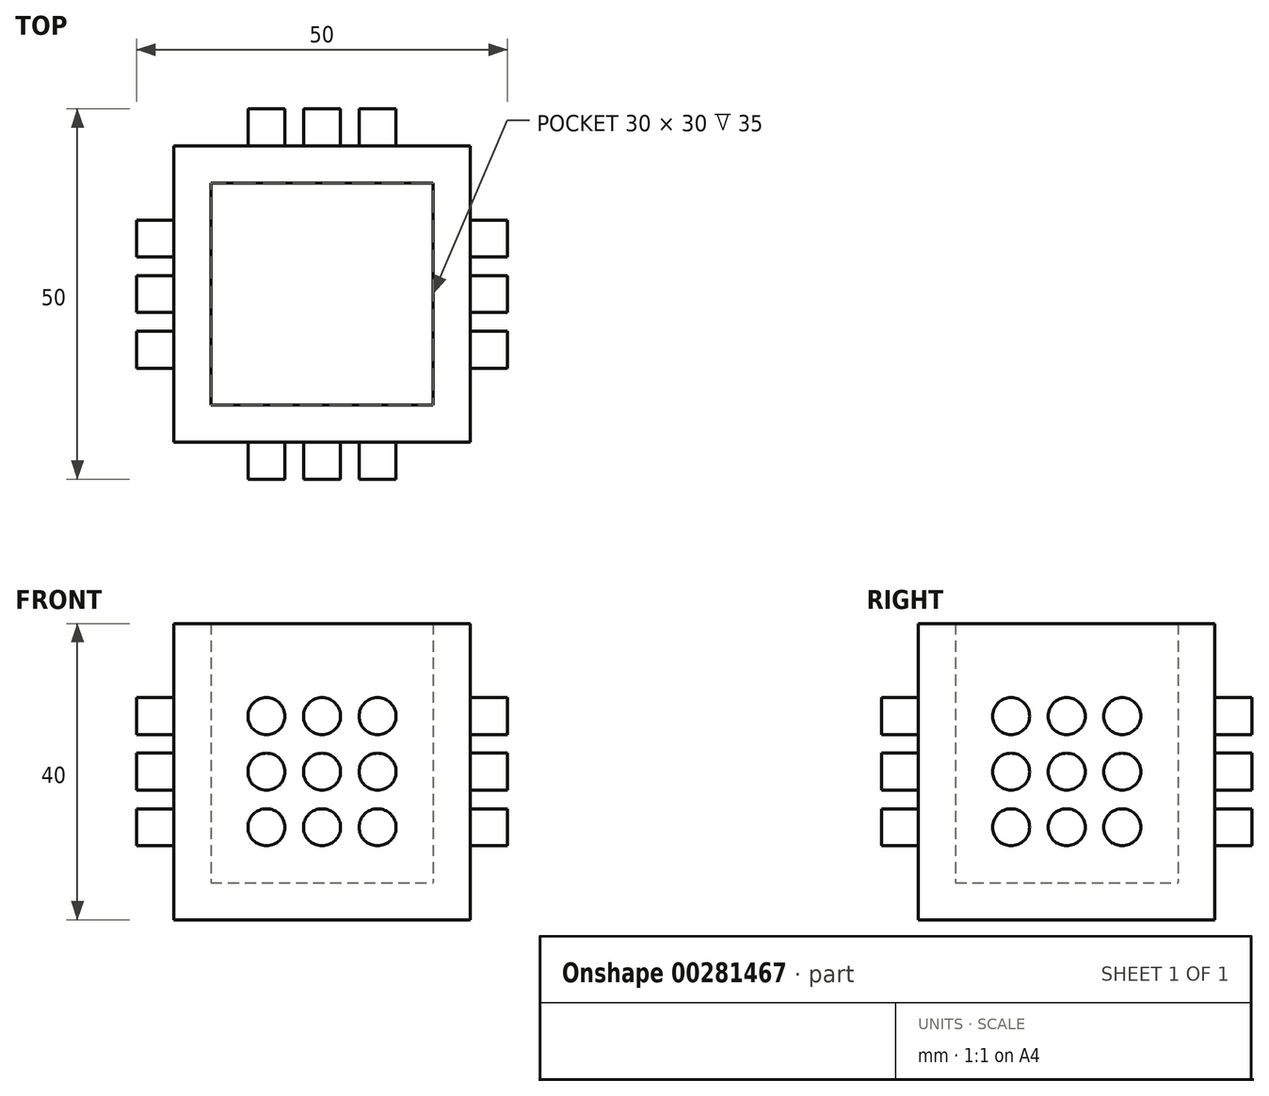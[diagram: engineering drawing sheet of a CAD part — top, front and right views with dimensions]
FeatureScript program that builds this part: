
annotation { "Feature Type Name" : "Feature", "Feature Type Description" : "" }
export const myFeature = defineFeature(function(context is Context, id is Id, definition is map)
    precondition{}
    {
        {
            var Q0;
            Q0=qCreatedBy(makeId("Top.planeOp"),FACE);
            var sketch = newSketch(context, id + "F0", { "sketchPlane" : qUnion([Q0])});
            skLineSegment(sketch, "E0.bottom", {"start": v(0, 0) * mm, "end": v(40, 0) * mm});
            skLineSegment(sketch, "E0.top", {"start": v(0, 40) * mm, "end": v(40, 40) * mm});
            skLineSegment(sketch, "E0.left", {"start": v(0, 0) * mm, "end": v(0, 40) * mm});
            skLineSegment(sketch, "E0.right", {"start": v(40, 0) * mm, "end": v(40, 40) * mm});
            skLineSegment(sketch, "E1.bottom", {"start": v(5, 5) * mm, "end": v(35, 5) * mm});
            skLineSegment(sketch, "E1.top", {"start": v(5, 35) * mm, "end": v(35, 35) * mm});
            skLineSegment(sketch, "E1.left", {"start": v(5, 5) * mm, "end": v(5, 35) * mm});
            skLineSegment(sketch, "E1.right", {"start": v(35, 5) * mm, "end": v(35, 35) * mm});
            skSolve(sketch);
        }
        {
            var Q0;
            Q0=makeQuery(id+"F0.imprint","IMPRINT",FACE,{"disambiguationData":[TD([[makeQuery(id+"F0.imprint","IMPRINT",EDGE,{"derivedFrom":sQuery(id+"F0.wireOp",EDGE,"E0.bottom")}),1.0]])]});
            var Q1;
            Q1=makeQuery(id+"F0.imprint","IMPRINT",FACE,{"disambiguationData":[TD([[makeQuery(id+"F0.imprint","IMPRINT",EDGE,{"derivedFrom":sQuery(id+"F0.wireOp",EDGE,"E1.bottom")}),1.0]])]});
            extrude(context, id + "F1", {"entities" : qUnion([Q0, Q1]), "depth" : 5 * mm});
        }
        {
            var Q0;
            Q0=makeQuery(id+"F1.opExtrude","CAP_FACE",FACE,{"disambiguationData":[OSD([sQuery(id+"F0.wireOp",EDGE,"E0.bottom"),sQuery(id+"F0.wireOp",EDGE,"E0.top"),sQuery(id+"F0.wireOp",EDGE,"E0.left"),sQuery(id+"F0.wireOp",EDGE,"E0.right")])],"isStart":false});
            var sketch = newSketch(context, id + "F2", { "sketchPlane" : qUnion([Q0])});
            skLineSegment(sketch, "E2.bottom", {"start": v(5, 5) * mm, "end": v(35, 5) * mm});
            skLineSegment(sketch, "E2.top", {"start": v(5, 35) * mm, "end": v(35, 35) * mm});
            skLineSegment(sketch, "E2.left", {"start": v(5, 5) * mm, "end": v(5, 35) * mm});
            skLineSegment(sketch, "E2.right", {"start": v(35, 5) * mm, "end": v(35, 35) * mm});
            skSolve(sketch);
        }
        {
            var Q0;
            Q0=makeQuery(id+"F2.imprint","IMPRINT",FACE,{"disambiguationData":[TD([[makeQuery(id+"F2.imprint","IMPRINT",EDGE,{"derivedFrom":sQuery(id+"F2.wireOp",EDGE,"E2.bottom")}),-1.0]])]});
            extrude(context, id + "F3", {"entities" : qUnion([Q0]), "operationType" : NewBodyOperationType.ADD, "depth" : 35 * mm});
        }
        {
            var Q0;
            Q0=qCreatedBy(makeId("Front.planeOp"),FACE);
            var sketch = newSketch(context, id + "F4", { "sketchPlane" : qUnion([Q0])});
            skLineSegment(sketch, "E3.bottom", {"start": v(5, 5) * mm, "end": v(35, 5) * mm});
            skLineSegment(sketch, "E3.top", {"start": v(5, 35) * mm, "end": v(35, 35) * mm});
            skLineSegment(sketch, "E3.left", {"start": v(5, 5) * mm, "end": v(5, 35) * mm});
            skLineSegment(sketch, "E3.right", {"start": v(35, 5) * mm, "end": v(35, 35) * mm});
            skLineSegment(sketch, "E4", {"start": v(12.5, 5) * mm, "end": v(12.5, 10) * mm});
            skLineSegment(sketch, "E5", {"start": v(20, 5) * mm, "end": v(20, 10) * mm});
            skLineSegment(sketch, "E6", {"start": v(27.5, 5) * mm, "end": v(27.5, 10) * mm});
            skLineSegment(sketch, "E7", {"start": v(5, 27.5) * mm, "end": v(10, 27.5) * mm});
            skLineSegment(sketch, "E8", {"start": v(5, 20) * mm, "end": v(10, 20) * mm});
            skLineSegment(sketch, "E9", {"start": v(5, 12.5) * mm, "end": v(10, 12.5) * mm});
            skCircle(sketch, "E10", {"center": v(12.5, 27.5) * mm, "radius": 2.5 * mm});
            skCircle(sketch, "E11", {"center": v(20, 27.5) * mm, "radius": 2.5 * mm});
            skCircle(sketch, "E12", {"center": v(27.5, 27.5) * mm, "radius": 2.5 * mm});
            skCircle(sketch, "E13", {"center": v(27.5, 20) * mm, "radius": 2.5 * mm});
            skCircle(sketch, "E14", {"center": v(20, 20) * mm, "radius": 2.5 * mm});
            skCircle(sketch, "E15", {"center": v(12.5, 20) * mm, "radius": 2.5 * mm});
            skCircle(sketch, "E16", {"center": v(12.5, 12.5) * mm, "radius": 2.5 * mm});
            skCircle(sketch, "E17", {"center": v(20, 12.5) * mm, "radius": 2.5 * mm});
            skCircle(sketch, "E18", {"center": v(27.5, 12.5) * mm, "radius": 2.5 * mm});
            skLineSegment(sketch, "E19.trimOffspring", {"start": v(12.5, 30) * mm, "end": v(12.5, 35) * mm});
            skLineSegment(sketch, "E20.trimOffspring", {"start": v(15, 27.5) * mm, "end": v(17.5, 27.5) * mm});
            skLineSegment(sketch, "E21.trimOffspring", {"start": v(22.5, 27.5) * mm, "end": v(25, 27.5) * mm});
            skLineSegment(sketch, "E22.trimOffspring", {"start": v(20, 30) * mm, "end": v(20, 35) * mm});
            skLineSegment(sketch, "E23.trimOffspring", {"start": v(30, 27.5) * mm, "end": v(35, 27.5) * mm});
            skLineSegment(sketch, "E24.trimOffspring", {"start": v(27.5, 30) * mm, "end": v(27.5, 35) * mm});
            skLineSegment(sketch, "E25.trimOffspring", {"start": v(12.5, 22.5) * mm, "end": v(12.5, 25) * mm});
            skLineSegment(sketch, "E26.trimOffspring", {"start": v(15, 20) * mm, "end": v(17.5, 20) * mm});
            skLineSegment(sketch, "E27.trimOffspring", {"start": v(22.5, 20) * mm, "end": v(25, 20) * mm});
            skLineSegment(sketch, "E28.trimOffspring", {"start": v(20, 22.5) * mm, "end": v(20, 25) * mm});
            skLineSegment(sketch, "E29.trimOffspring", {"start": v(30, 20) * mm, "end": v(35, 20) * mm});
            skLineSegment(sketch, "E30.trimOffspring", {"start": v(27.5, 22.5) * mm, "end": v(27.5, 25) * mm});
            skLineSegment(sketch, "E31.trimOffspring", {"start": v(12.5, 15) * mm, "end": v(12.5, 17.5) * mm});
            skLineSegment(sketch, "E32.trimOffspring", {"start": v(15, 12.5) * mm, "end": v(17.5, 12.5) * mm});
            skLineSegment(sketch, "E33.trimOffspring", {"start": v(22.5, 12.5) * mm, "end": v(25, 12.5) * mm});
            skLineSegment(sketch, "E34.trimOffspring", {"start": v(20, 15) * mm, "end": v(20, 17.5) * mm});
            skLineSegment(sketch, "E35.trimOffspring", {"start": v(30, 12.5) * mm, "end": v(35, 12.5) * mm});
            skLineSegment(sketch, "E36.trimOffspring", {"start": v(27.5, 15) * mm, "end": v(27.5, 17.5) * mm});
            skSolve(sketch);
        }
        {
            var Q0;
            {var subQ0=sQuery(id+"F0.wireOp",EDGE,"E0.right");Q0=makeQuery(id+"F3.boolean.opBoolean","MERGE",FACE,{"derivedFrom":[makeQuery(id+"F1.opExtrude","SWEPT_FACE",FACE,{"disambiguationData":[OSD([subQ0])]}),makeQuery(id+"F3.opExtrude","SWEPT_FACE",FACE,{"disambiguationData":[OSD([subQ0])]})]});}
            var sketch = newSketch(context, id + "F5", { "sketchPlane" : qUnion([Q0])});
            skLineSegment(sketch, "E37.bottom", {"start": v(5, 5) * mm, "end": v(35, 5) * mm});
            skLineSegment(sketch, "E37.top", {"start": v(5, 35) * mm, "end": v(35, 35) * mm});
            skLineSegment(sketch, "E37.left", {"start": v(5, 5) * mm, "end": v(5, 35) * mm});
            skLineSegment(sketch, "E37.right", {"start": v(35, 5) * mm, "end": v(35, 35) * mm});
            skLineSegment(sketch, "E38", {"start": v(12.5, 5) * mm, "end": v(12.5, 10) * mm});
            skLineSegment(sketch, "E39", {"start": v(20, 5) * mm, "end": v(20, 10) * mm});
            skLineSegment(sketch, "E40", {"start": v(27.5, 5) * mm, "end": v(27.5, 10) * mm});
            skLineSegment(sketch, "E41", {"start": v(5, 27.5) * mm, "end": v(10, 27.5) * mm});
            skLineSegment(sketch, "E42", {"start": v(5, 20) * mm, "end": v(10, 20) * mm});
            skLineSegment(sketch, "E43", {"start": v(5, 12.5) * mm, "end": v(10, 12.5) * mm});
            skCircle(sketch, "E44", {"center": v(12.5, 27.5) * mm, "radius": 2.5 * mm});
            skCircle(sketch, "E45", {"center": v(20, 27.5) * mm, "radius": 2.5 * mm});
            skCircle(sketch, "E46", {"center": v(27.5, 27.5) * mm, "radius": 2.5 * mm});
            skCircle(sketch, "E47", {"center": v(27.5, 20) * mm, "radius": 2.5 * mm});
            skCircle(sketch, "E48", {"center": v(20, 20) * mm, "radius": 2.5 * mm});
            skCircle(sketch, "E49", {"center": v(12.5, 20) * mm, "radius": 2.5 * mm});
            skCircle(sketch, "E50", {"center": v(12.5, 12.5) * mm, "radius": 2.5 * mm});
            skCircle(sketch, "E51", {"center": v(20, 12.5) * mm, "radius": 2.5 * mm});
            skCircle(sketch, "E52", {"center": v(27.5, 12.5) * mm, "radius": 2.5 * mm});
            skLineSegment(sketch, "E53.trimOffspring", {"start": v(12.5, 30) * mm, "end": v(12.5, 35) * mm});
            skLineSegment(sketch, "E54.trimOffspring", {"start": v(15, 27.5) * mm, "end": v(17.5, 27.5) * mm});
            skLineSegment(sketch, "E55.trimOffspring", {"start": v(22.5, 27.5) * mm, "end": v(25, 27.5) * mm});
            skLineSegment(sketch, "E56.trimOffspring", {"start": v(20, 30) * mm, "end": v(20, 35) * mm});
            skLineSegment(sketch, "E57.trimOffspring", {"start": v(30, 27.5) * mm, "end": v(35, 27.5) * mm});
            skLineSegment(sketch, "E58.trimOffspring", {"start": v(27.5, 30) * mm, "end": v(27.5, 35) * mm});
            skLineSegment(sketch, "E59.trimOffspring", {"start": v(12.5, 22.5) * mm, "end": v(12.5, 25) * mm});
            skLineSegment(sketch, "E60.trimOffspring", {"start": v(15, 20) * mm, "end": v(17.5, 20) * mm});
            skLineSegment(sketch, "E61.trimOffspring", {"start": v(22.5, 20) * mm, "end": v(25, 20) * mm});
            skLineSegment(sketch, "E62.trimOffspring", {"start": v(20, 22.5) * mm, "end": v(20, 25) * mm});
            skLineSegment(sketch, "E63.trimOffspring", {"start": v(30, 20) * mm, "end": v(35, 20) * mm});
            skLineSegment(sketch, "E64.trimOffspring", {"start": v(27.5, 22.5) * mm, "end": v(27.5, 25) * mm});
            skLineSegment(sketch, "E65.trimOffspring", {"start": v(12.5, 15) * mm, "end": v(12.5, 17.5) * mm});
            skLineSegment(sketch, "E66.trimOffspring", {"start": v(15, 12.5) * mm, "end": v(17.5, 12.5) * mm});
            skLineSegment(sketch, "E67.trimOffspring", {"start": v(22.5, 12.5) * mm, "end": v(25, 12.5) * mm});
            skLineSegment(sketch, "E68.trimOffspring", {"start": v(20, 15) * mm, "end": v(20, 17.5) * mm});
            skLineSegment(sketch, "E69.trimOffspring", {"start": v(30, 12.5) * mm, "end": v(35, 12.5) * mm});
            skLineSegment(sketch, "E70.trimOffspring", {"start": v(27.5, 15) * mm, "end": v(27.5, 17.5) * mm});
            skSolve(sketch);
        }
        {
            var Q0;
            {var subQ0=sQuery(id+"F0.wireOp",EDGE,"E0.top");Q0=makeQuery(id+"F3.boolean.opBoolean","MERGE",FACE,{"derivedFrom":[makeQuery(id+"F1.opExtrude","SWEPT_FACE",FACE,{"disambiguationData":[OSD([subQ0])]}),makeQuery(id+"F3.opExtrude","SWEPT_FACE",FACE,{"disambiguationData":[OSD([subQ0])]})]});}
            var sketch = newSketch(context, id + "F6", { "sketchPlane" : qUnion([Q0])});
            skLineSegment(sketch, "E71.bottom", {"start": v(-35, 5) * mm, "end": v(-5, 5) * mm});
            skLineSegment(sketch, "E71.top", {"start": v(-35, 35) * mm, "end": v(-5, 35) * mm});
            skLineSegment(sketch, "E71.left", {"start": v(-35, 5) * mm, "end": v(-35, 35) * mm});
            skLineSegment(sketch, "E71.right", {"start": v(-5, 5) * mm, "end": v(-5, 35) * mm});
            skLineSegment(sketch, "E72", {"start": v(-27.5, 5) * mm, "end": v(-27.5, 10) * mm});
            skLineSegment(sketch, "E73", {"start": v(-20, 5) * mm, "end": v(-20, 10) * mm});
            skLineSegment(sketch, "E74", {"start": v(-12.5, 5) * mm, "end": v(-12.5, 10) * mm});
            skLineSegment(sketch, "E75", {"start": v(-35, 27.5) * mm, "end": v(-30, 27.5) * mm});
            skLineSegment(sketch, "E76", {"start": v(-35, 20) * mm, "end": v(-30, 20) * mm});
            skLineSegment(sketch, "E77", {"start": v(-35, 12.5) * mm, "end": v(-30, 12.5) * mm});
            skCircle(sketch, "E78", {"center": v(-27.5, 27.5) * mm, "radius": 2.5 * mm});
            skCircle(sketch, "E79", {"center": v(-20, 27.5) * mm, "radius": 2.5 * mm});
            skCircle(sketch, "E80", {"center": v(-12.5, 27.5) * mm, "radius": 2.5 * mm});
            skCircle(sketch, "E81", {"center": v(-12.5, 20) * mm, "radius": 2.5 * mm});
            skCircle(sketch, "E82", {"center": v(-20, 20) * mm, "radius": 2.5 * mm});
            skCircle(sketch, "E83", {"center": v(-27.5, 20) * mm, "radius": 2.5 * mm});
            skCircle(sketch, "E84", {"center": v(-27.5, 12.5) * mm, "radius": 2.5 * mm});
            skCircle(sketch, "E85", {"center": v(-20, 12.5) * mm, "radius": 2.5 * mm});
            skCircle(sketch, "E86", {"center": v(-12.5, 12.5) * mm, "radius": 2.5 * mm});
            skLineSegment(sketch, "E87.trimOffspring", {"start": v(-27.5, 30) * mm, "end": v(-27.5, 35) * mm});
            skLineSegment(sketch, "E88.trimOffspring", {"start": v(-25, 27.5) * mm, "end": v(-22.5, 27.5) * mm});
            skLineSegment(sketch, "E89.trimOffspring", {"start": v(-17.5, 27.5) * mm, "end": v(-15, 27.5) * mm});
            skLineSegment(sketch, "E90.trimOffspring", {"start": v(-20, 30) * mm, "end": v(-20, 35) * mm});
            skLineSegment(sketch, "E91.trimOffspring", {"start": v(-10, 27.5) * mm, "end": v(-5, 27.5) * mm});
            skLineSegment(sketch, "E92.trimOffspring", {"start": v(-12.5, 30) * mm, "end": v(-12.5, 35) * mm});
            skLineSegment(sketch, "E93.trimOffspring", {"start": v(-27.5, 22.5) * mm, "end": v(-27.5, 25) * mm});
            skLineSegment(sketch, "E94.trimOffspring", {"start": v(-25, 20) * mm, "end": v(-22.5, 20) * mm});
            skLineSegment(sketch, "E95.trimOffspring", {"start": v(-17.5, 20) * mm, "end": v(-15, 20) * mm});
            skLineSegment(sketch, "E96.trimOffspring", {"start": v(-20, 22.5) * mm, "end": v(-20, 25) * mm});
            skLineSegment(sketch, "E97.trimOffspring", {"start": v(-10, 20) * mm, "end": v(-5, 20) * mm});
            skLineSegment(sketch, "E98.trimOffspring", {"start": v(-12.5, 22.5) * mm, "end": v(-12.5, 25) * mm});
            skLineSegment(sketch, "E99.trimOffspring", {"start": v(-27.5, 15) * mm, "end": v(-27.5, 17.5) * mm});
            skLineSegment(sketch, "E100.trimOffspring", {"start": v(-25, 12.5) * mm, "end": v(-22.5, 12.5) * mm});
            skLineSegment(sketch, "E101.trimOffspring", {"start": v(-17.5, 12.5) * mm, "end": v(-15, 12.5) * mm});
            skLineSegment(sketch, "E102.trimOffspring", {"start": v(-20, 15) * mm, "end": v(-20, 17.5) * mm});
            skLineSegment(sketch, "E103.trimOffspring", {"start": v(-10, 12.5) * mm, "end": v(-5, 12.5) * mm});
            skLineSegment(sketch, "E104.trimOffspring", {"start": v(-12.5, 15) * mm, "end": v(-12.5, 17.5) * mm});
            skSolve(sketch);
        }
        {
            var Q0;
            {var subQ0=sQuery(id+"F0.wireOp",EDGE,"E0.left");Q0=makeQuery(id+"F3.boolean.opBoolean","MERGE",FACE,{"derivedFrom":[makeQuery(id+"F1.opExtrude","SWEPT_FACE",FACE,{"disambiguationData":[OSD([subQ0])]}),makeQuery(id+"F3.opExtrude","SWEPT_FACE",FACE,{"disambiguationData":[OSD([subQ0])]})]});}
            var sketch = newSketch(context, id + "F7", { "sketchPlane" : qUnion([Q0])});
            skLineSegment(sketch, "E105.bottom", {"start": v(-35, 5) * mm, "end": v(-5, 5) * mm});
            skLineSegment(sketch, "E105.top", {"start": v(-35, 35) * mm, "end": v(-5, 35) * mm});
            skLineSegment(sketch, "E105.left", {"start": v(-35, 5) * mm, "end": v(-35, 35) * mm});
            skLineSegment(sketch, "E105.right", {"start": v(-5, 5) * mm, "end": v(-5, 35) * mm});
            skLineSegment(sketch, "E106", {"start": v(-27.5, 5) * mm, "end": v(-27.5, 10) * mm});
            skLineSegment(sketch, "E107", {"start": v(-20, 5) * mm, "end": v(-20, 10) * mm});
            skLineSegment(sketch, "E108", {"start": v(-12.5, 5) * mm, "end": v(-12.5, 10) * mm});
            skLineSegment(sketch, "E109", {"start": v(-35, 27.5) * mm, "end": v(-30, 27.5) * mm});
            skLineSegment(sketch, "E110", {"start": v(-35, 20) * mm, "end": v(-30, 20) * mm});
            skLineSegment(sketch, "E111", {"start": v(-35, 12.5) * mm, "end": v(-30, 12.5) * mm});
            skCircle(sketch, "E112", {"center": v(-27.5, 27.5) * mm, "radius": 2.5 * mm});
            skCircle(sketch, "E113", {"center": v(-20, 27.5) * mm, "radius": 2.5 * mm});
            skCircle(sketch, "E114", {"center": v(-12.5, 27.5) * mm, "radius": 2.5 * mm});
            skCircle(sketch, "E115", {"center": v(-12.5, 20) * mm, "radius": 2.5 * mm});
            skCircle(sketch, "E116", {"center": v(-20, 20) * mm, "radius": 2.5 * mm});
            skCircle(sketch, "E117", {"center": v(-27.5, 20) * mm, "radius": 2.5 * mm});
            skCircle(sketch, "E118", {"center": v(-27.5, 12.5) * mm, "radius": 2.5 * mm});
            skCircle(sketch, "E119", {"center": v(-20, 12.5) * mm, "radius": 2.5 * mm});
            skCircle(sketch, "E120", {"center": v(-12.5, 12.5) * mm, "radius": 2.5 * mm});
            skLineSegment(sketch, "E121.trimOffspring", {"start": v(-27.5, 30) * mm, "end": v(-27.5, 35) * mm});
            skLineSegment(sketch, "E122.trimOffspring", {"start": v(-25, 27.5) * mm, "end": v(-22.5, 27.5) * mm});
            skLineSegment(sketch, "E123.trimOffspring", {"start": v(-17.5, 27.5) * mm, "end": v(-15, 27.5) * mm});
            skLineSegment(sketch, "E124.trimOffspring", {"start": v(-20, 30) * mm, "end": v(-20, 35) * mm});
            skLineSegment(sketch, "E125.trimOffspring", {"start": v(-10, 27.5) * mm, "end": v(-5, 27.5) * mm});
            skLineSegment(sketch, "E126.trimOffspring", {"start": v(-12.5, 30) * mm, "end": v(-12.5, 35) * mm});
            skLineSegment(sketch, "E127.trimOffspring", {"start": v(-27.5, 22.5) * mm, "end": v(-27.5, 25) * mm});
            skLineSegment(sketch, "E128.trimOffspring", {"start": v(-25, 20) * mm, "end": v(-22.5, 20) * mm});
            skLineSegment(sketch, "E129.trimOffspring", {"start": v(-17.5, 20) * mm, "end": v(-15, 20) * mm});
            skLineSegment(sketch, "E130.trimOffspring", {"start": v(-20, 22.5) * mm, "end": v(-20, 25) * mm});
            skLineSegment(sketch, "E131.trimOffspring", {"start": v(-10, 20) * mm, "end": v(-5, 20) * mm});
            skLineSegment(sketch, "E132.trimOffspring", {"start": v(-12.5, 22.5) * mm, "end": v(-12.5, 25) * mm});
            skLineSegment(sketch, "E133.trimOffspring", {"start": v(-27.5, 15) * mm, "end": v(-27.5, 17.5) * mm});
            skLineSegment(sketch, "E134.trimOffspring", {"start": v(-25, 12.5) * mm, "end": v(-22.5, 12.5) * mm});
            skLineSegment(sketch, "E135.trimOffspring", {"start": v(-17.5, 12.5) * mm, "end": v(-15, 12.5) * mm});
            skLineSegment(sketch, "E136.trimOffspring", {"start": v(-20, 15) * mm, "end": v(-20, 17.5) * mm});
            skLineSegment(sketch, "E137.trimOffspring", {"start": v(-10, 12.5) * mm, "end": v(-5, 12.5) * mm});
            skLineSegment(sketch, "E138.trimOffspring", {"start": v(-12.5, 15) * mm, "end": v(-12.5, 17.5) * mm});
            skSolve(sketch);
        }
        {
            var Q0;
            {var subQ0=sQuery(id+"F7.wireOp",EDGE,"E112");var subQ1=makeQuery(id+"F7.imprint","INTERSECT",VERTEX,{"derivedFrom":[subQ0,sQuery(id+"F7.wireOp",EDGE,"E121.trimOffspring")]});Q0=makeQuery(id+"F7.imprint","IMPRINT",FACE,{"disambiguationData":[TD([[makeQuery(id+"F7.imprint","IMPRINT",EDGE,{"disambiguationData":[TD([[subQ1,1.0]])],"derivedFrom":subQ0}),1.0]])]});}
            var Q1;
            {var subQ0=sQuery(id+"F7.wireOp",EDGE,"E113");var subQ1=makeQuery(id+"F7.imprint","INTERSECT",VERTEX,{"derivedFrom":[subQ0,sQuery(id+"F7.wireOp",EDGE,"E123.trimOffspring")]});Q1=makeQuery(id+"F7.imprint","IMPRINT",FACE,{"disambiguationData":[TD([[makeQuery(id+"F7.imprint","IMPRINT",EDGE,{"disambiguationData":[TD([[subQ1,-1.0]])],"derivedFrom":subQ0}),1.0]])]});}
            var Q2;
            {var subQ0=sQuery(id+"F7.wireOp",EDGE,"E114");var subQ1=makeQuery(id+"F7.imprint","INTERSECT",VERTEX,{"derivedFrom":[subQ0,sQuery(id+"F7.wireOp",EDGE,"E125.trimOffspring")]});Q2=makeQuery(id+"F7.imprint","IMPRINT",FACE,{"disambiguationData":[TD([[makeQuery(id+"F7.imprint","IMPRINT",EDGE,{"disambiguationData":[TD([[subQ1,-1.0]])],"derivedFrom":subQ0}),1.0]])]});}
            var Q3;
            {var subQ0=sQuery(id+"F7.wireOp",EDGE,"E120");var subQ1=makeQuery(id+"F7.imprint","INTERSECT",VERTEX,{"derivedFrom":[subQ0,sQuery(id+"F7.wireOp",EDGE,"E137.trimOffspring")]});Q3=makeQuery(id+"F7.imprint","IMPRINT",FACE,{"disambiguationData":[TD([[makeQuery(id+"F7.imprint","IMPRINT",EDGE,{"disambiguationData":[TD([[subQ1,-1.0]])],"derivedFrom":subQ0}),1.0]])]});}
            var Q4;
            {var subQ0=sQuery(id+"F7.wireOp",EDGE,"E119");var subQ1=makeQuery(id+"F7.imprint","INTERSECT",VERTEX,{"derivedFrom":[subQ0,sQuery(id+"F7.wireOp",EDGE,"E135.trimOffspring")]});Q4=makeQuery(id+"F7.imprint","IMPRINT",FACE,{"disambiguationData":[TD([[makeQuery(id+"F7.imprint","IMPRINT",EDGE,{"disambiguationData":[TD([[subQ1,-1.0]])],"derivedFrom":subQ0}),1.0]])]});}
            var Q5;
            {var subQ0=sQuery(id+"F7.wireOp",EDGE,"E118");var subQ1=makeQuery(id+"F7.imprint","INTERSECT",VERTEX,{"derivedFrom":[subQ0,sQuery(id+"F7.wireOp",EDGE,"E133.trimOffspring")]});Q5=makeQuery(id+"F7.imprint","IMPRINT",FACE,{"disambiguationData":[TD([[makeQuery(id+"F7.imprint","IMPRINT",EDGE,{"disambiguationData":[TD([[subQ1,1.0]])],"derivedFrom":subQ0}),1.0]])]});}
            var Q6;
            {var subQ0=sQuery(id+"F7.wireOp",EDGE,"E117");var subQ1=makeQuery(id+"F7.imprint","INTERSECT",VERTEX,{"derivedFrom":[subQ0,sQuery(id+"F7.wireOp",EDGE,"E127.trimOffspring")]});Q6=makeQuery(id+"F7.imprint","IMPRINT",FACE,{"disambiguationData":[TD([[makeQuery(id+"F7.imprint","IMPRINT",EDGE,{"disambiguationData":[TD([[subQ1,1.0]])],"derivedFrom":subQ0}),1.0]])]});}
            var Q7;
            {var subQ0=sQuery(id+"F7.wireOp",EDGE,"E115");var subQ1=makeQuery(id+"F7.imprint","INTERSECT",VERTEX,{"derivedFrom":[subQ0,sQuery(id+"F7.wireOp",EDGE,"E131.trimOffspring")]});Q7=makeQuery(id+"F7.imprint","IMPRINT",FACE,{"disambiguationData":[TD([[makeQuery(id+"F7.imprint","IMPRINT",EDGE,{"disambiguationData":[TD([[subQ1,-1.0]])],"derivedFrom":subQ0}),1.0]])]});}
            var Q8;
            {var subQ0=sQuery(id+"F7.wireOp",EDGE,"E116");var subQ1=makeQuery(id+"F7.imprint","INTERSECT",VERTEX,{"derivedFrom":[subQ0,sQuery(id+"F7.wireOp",EDGE,"E129.trimOffspring")]});Q8=makeQuery(id+"F7.imprint","IMPRINT",FACE,{"disambiguationData":[TD([[makeQuery(id+"F7.imprint","IMPRINT",EDGE,{"disambiguationData":[TD([[subQ1,-1.0]])],"derivedFrom":subQ0}),1.0]])]});}
            extrude(context, id + "F8", {"entities" : qUnion([Q0, Q1, Q2, Q3, Q4, Q5, Q6, Q7, Q8]), "operationType" : NewBodyOperationType.ADD, "depth" : 5 * mm});
        }
        {
            var Q0;
            {var subQ0=sQuery(id+"F4.wireOp",EDGE,"E16");var subQ1=makeQuery(id+"F4.imprint","INTERSECT",VERTEX,{"derivedFrom":[subQ0,sQuery(id+"F4.wireOp",EDGE,"E31.trimOffspring")]});Q0=makeQuery(id+"F4.imprint","IMPRINT",FACE,{"disambiguationData":[TD([[makeQuery(id+"F4.imprint","IMPRINT",EDGE,{"disambiguationData":[TD([[subQ1,1.0]])],"derivedFrom":subQ0}),1.0]])]});}
            var Q1;
            {var subQ0=sQuery(id+"F4.wireOp",EDGE,"E17");var subQ1=makeQuery(id+"F4.imprint","INTERSECT",VERTEX,{"derivedFrom":[subQ0,sQuery(id+"F4.wireOp",EDGE,"E33.trimOffspring")]});Q1=makeQuery(id+"F4.imprint","IMPRINT",FACE,{"disambiguationData":[TD([[makeQuery(id+"F4.imprint","IMPRINT",EDGE,{"disambiguationData":[TD([[subQ1,-1.0]])],"derivedFrom":subQ0}),1.0]])]});}
            var Q2;
            {var subQ0=sQuery(id+"F4.wireOp",EDGE,"E18");var subQ1=makeQuery(id+"F4.imprint","INTERSECT",VERTEX,{"derivedFrom":[subQ0,sQuery(id+"F4.wireOp",EDGE,"E35.trimOffspring")]});Q2=makeQuery(id+"F4.imprint","IMPRINT",FACE,{"disambiguationData":[TD([[makeQuery(id+"F4.imprint","IMPRINT",EDGE,{"disambiguationData":[TD([[subQ1,-1.0]])],"derivedFrom":subQ0}),1.0]])]});}
            var Q3;
            {var subQ0=sQuery(id+"F4.wireOp",EDGE,"E13");var subQ1=makeQuery(id+"F4.imprint","INTERSECT",VERTEX,{"derivedFrom":[subQ0,sQuery(id+"F4.wireOp",EDGE,"E29.trimOffspring")]});Q3=makeQuery(id+"F4.imprint","IMPRINT",FACE,{"disambiguationData":[TD([[makeQuery(id+"F4.imprint","IMPRINT",EDGE,{"disambiguationData":[TD([[subQ1,-1.0]])],"derivedFrom":subQ0}),1.0]])]});}
            var Q4;
            {var subQ0=sQuery(id+"F4.wireOp",EDGE,"E14");var subQ1=makeQuery(id+"F4.imprint","INTERSECT",VERTEX,{"derivedFrom":[subQ0,sQuery(id+"F4.wireOp",EDGE,"E27.trimOffspring")]});Q4=makeQuery(id+"F4.imprint","IMPRINT",FACE,{"disambiguationData":[TD([[makeQuery(id+"F4.imprint","IMPRINT",EDGE,{"disambiguationData":[TD([[subQ1,-1.0]])],"derivedFrom":subQ0}),1.0]])]});}
            var Q5;
            {var subQ0=sQuery(id+"F4.wireOp",EDGE,"E15");var subQ1=makeQuery(id+"F4.imprint","INTERSECT",VERTEX,{"derivedFrom":[subQ0,sQuery(id+"F4.wireOp",EDGE,"E25.trimOffspring")]});Q5=makeQuery(id+"F4.imprint","IMPRINT",FACE,{"disambiguationData":[TD([[makeQuery(id+"F4.imprint","IMPRINT",EDGE,{"disambiguationData":[TD([[subQ1,1.0]])],"derivedFrom":subQ0}),1.0]])]});}
            var Q6;
            {var subQ0=sQuery(id+"F4.wireOp",EDGE,"E10");var subQ1=makeQuery(id+"F4.imprint","INTERSECT",VERTEX,{"derivedFrom":[subQ0,sQuery(id+"F4.wireOp",EDGE,"E19.trimOffspring")]});Q6=makeQuery(id+"F4.imprint","IMPRINT",FACE,{"disambiguationData":[TD([[makeQuery(id+"F4.imprint","IMPRINT",EDGE,{"disambiguationData":[TD([[subQ1,1.0]])],"derivedFrom":subQ0}),1.0]])]});}
            var Q7;
            {var subQ0=sQuery(id+"F4.wireOp",EDGE,"E11");var subQ1=makeQuery(id+"F4.imprint","INTERSECT",VERTEX,{"derivedFrom":[subQ0,sQuery(id+"F4.wireOp",EDGE,"E21.trimOffspring")]});Q7=makeQuery(id+"F4.imprint","IMPRINT",FACE,{"disambiguationData":[TD([[makeQuery(id+"F4.imprint","IMPRINT",EDGE,{"disambiguationData":[TD([[subQ1,-1.0]])],"derivedFrom":subQ0}),1.0]])]});}
            var Q8;
            {var subQ0=sQuery(id+"F4.wireOp",EDGE,"E12");var subQ1=makeQuery(id+"F4.imprint","INTERSECT",VERTEX,{"derivedFrom":[subQ0,sQuery(id+"F4.wireOp",EDGE,"E23.trimOffspring")]});Q8=makeQuery(id+"F4.imprint","IMPRINT",FACE,{"disambiguationData":[TD([[makeQuery(id+"F4.imprint","IMPRINT",EDGE,{"disambiguationData":[TD([[subQ1,-1.0]])],"derivedFrom":subQ0}),1.0]])]});}
            extrude(context, id + "F9", {"entities" : qUnion([Q0, Q1, Q2, Q3, Q4, Q5, Q6, Q7, Q8]), "operationType" : NewBodyOperationType.ADD, "depth" : 5 * mm});
        }
        {
            var Q0;
            {var subQ0=sQuery(id+"F6.wireOp",EDGE,"E84");var subQ1=makeQuery(id+"F6.imprint","INTERSECT",VERTEX,{"derivedFrom":[subQ0,sQuery(id+"F6.wireOp",EDGE,"E99.trimOffspring")]});Q0=makeQuery(id+"F6.imprint","IMPRINT",FACE,{"disambiguationData":[TD([[makeQuery(id+"F6.imprint","IMPRINT",EDGE,{"disambiguationData":[TD([[subQ1,1.0]])],"derivedFrom":subQ0}),1.0]])]});}
            var Q1;
            {var subQ0=sQuery(id+"F6.wireOp",EDGE,"E83");var subQ1=makeQuery(id+"F6.imprint","INTERSECT",VERTEX,{"derivedFrom":[subQ0,sQuery(id+"F6.wireOp",EDGE,"E93.trimOffspring")]});Q1=makeQuery(id+"F6.imprint","IMPRINT",FACE,{"disambiguationData":[TD([[makeQuery(id+"F6.imprint","IMPRINT",EDGE,{"disambiguationData":[TD([[subQ1,1.0]])],"derivedFrom":subQ0}),1.0]])]});}
            var Q2;
            {var subQ0=sQuery(id+"F6.wireOp",EDGE,"E78");var subQ1=makeQuery(id+"F6.imprint","INTERSECT",VERTEX,{"derivedFrom":[subQ0,sQuery(id+"F6.wireOp",EDGE,"E87.trimOffspring")]});Q2=makeQuery(id+"F6.imprint","IMPRINT",FACE,{"disambiguationData":[TD([[makeQuery(id+"F6.imprint","IMPRINT",EDGE,{"disambiguationData":[TD([[subQ1,1.0]])],"derivedFrom":subQ0}),1.0]])]});}
            var Q3;
            {var subQ0=sQuery(id+"F6.wireOp",EDGE,"E79");var subQ1=makeQuery(id+"F6.imprint","INTERSECT",VERTEX,{"derivedFrom":[subQ0,sQuery(id+"F6.wireOp",EDGE,"E89.trimOffspring")]});Q3=makeQuery(id+"F6.imprint","IMPRINT",FACE,{"disambiguationData":[TD([[makeQuery(id+"F6.imprint","IMPRINT",EDGE,{"disambiguationData":[TD([[subQ1,-1.0]])],"derivedFrom":subQ0}),1.0]])]});}
            var Q4;
            {var subQ0=sQuery(id+"F6.wireOp",EDGE,"E82");var subQ1=makeQuery(id+"F6.imprint","INTERSECT",VERTEX,{"derivedFrom":[subQ0,sQuery(id+"F6.wireOp",EDGE,"E95.trimOffspring")]});Q4=makeQuery(id+"F6.imprint","IMPRINT",FACE,{"disambiguationData":[TD([[makeQuery(id+"F6.imprint","IMPRINT",EDGE,{"disambiguationData":[TD([[subQ1,-1.0]])],"derivedFrom":subQ0}),1.0]])]});}
            var Q5;
            {var subQ0=sQuery(id+"F6.wireOp",EDGE,"E85");var subQ1=makeQuery(id+"F6.imprint","INTERSECT",VERTEX,{"derivedFrom":[subQ0,sQuery(id+"F6.wireOp",EDGE,"E101.trimOffspring")]});Q5=makeQuery(id+"F6.imprint","IMPRINT",FACE,{"disambiguationData":[TD([[makeQuery(id+"F6.imprint","IMPRINT",EDGE,{"disambiguationData":[TD([[subQ1,-1.0]])],"derivedFrom":subQ0}),1.0]])]});}
            var Q6;
            {var subQ0=sQuery(id+"F6.wireOp",EDGE,"E86");var subQ1=makeQuery(id+"F6.imprint","INTERSECT",VERTEX,{"derivedFrom":[subQ0,sQuery(id+"F6.wireOp",EDGE,"E103.trimOffspring")]});Q6=makeQuery(id+"F6.imprint","IMPRINT",FACE,{"disambiguationData":[TD([[makeQuery(id+"F6.imprint","IMPRINT",EDGE,{"disambiguationData":[TD([[subQ1,-1.0]])],"derivedFrom":subQ0}),1.0]])]});}
            var Q7;
            {var subQ0=sQuery(id+"F6.wireOp",EDGE,"E81");var subQ1=makeQuery(id+"F6.imprint","INTERSECT",VERTEX,{"derivedFrom":[subQ0,sQuery(id+"F6.wireOp",EDGE,"E97.trimOffspring")]});Q7=makeQuery(id+"F6.imprint","IMPRINT",FACE,{"disambiguationData":[TD([[makeQuery(id+"F6.imprint","IMPRINT",EDGE,{"disambiguationData":[TD([[subQ1,-1.0]])],"derivedFrom":subQ0}),1.0]])]});}
            var Q8;
            {var subQ0=sQuery(id+"F6.wireOp",EDGE,"E80");var subQ1=makeQuery(id+"F6.imprint","INTERSECT",VERTEX,{"derivedFrom":[subQ0,sQuery(id+"F6.wireOp",EDGE,"E91.trimOffspring")]});Q8=makeQuery(id+"F6.imprint","IMPRINT",FACE,{"disambiguationData":[TD([[makeQuery(id+"F6.imprint","IMPRINT",EDGE,{"disambiguationData":[TD([[subQ1,-1.0]])],"derivedFrom":subQ0}),1.0]])]});}
            extrude(context, id + "F10", {"entities" : qUnion([Q0, Q1, Q2, Q3, Q4, Q5, Q6, Q7, Q8]), "operationType" : NewBodyOperationType.ADD, "depth" : 5 * mm});
        }
        {
            var Q0;
            {var subQ0=sQuery(id+"F5.wireOp",EDGE,"E44");var subQ1=makeQuery(id+"F5.imprint","INTERSECT",VERTEX,{"derivedFrom":[subQ0,sQuery(id+"F5.wireOp",EDGE,"E53.trimOffspring")]});Q0=makeQuery(id+"F5.imprint","IMPRINT",FACE,{"disambiguationData":[TD([[makeQuery(id+"F5.imprint","IMPRINT",EDGE,{"disambiguationData":[TD([[subQ1,1.0]])],"derivedFrom":subQ0}),1.0]])]});}
            var Q1;
            {var subQ0=sQuery(id+"F5.wireOp",EDGE,"E45");var subQ1=makeQuery(id+"F5.imprint","INTERSECT",VERTEX,{"derivedFrom":[subQ0,sQuery(id+"F5.wireOp",EDGE,"E55.trimOffspring")]});Q1=makeQuery(id+"F5.imprint","IMPRINT",FACE,{"disambiguationData":[TD([[makeQuery(id+"F5.imprint","IMPRINT",EDGE,{"disambiguationData":[TD([[subQ1,-1.0]])],"derivedFrom":subQ0}),1.0]])]});}
            var Q2;
            {var subQ0=sQuery(id+"F5.wireOp",EDGE,"E46");var subQ1=makeQuery(id+"F5.imprint","INTERSECT",VERTEX,{"derivedFrom":[subQ0,sQuery(id+"F5.wireOp",EDGE,"E57.trimOffspring")]});Q2=makeQuery(id+"F5.imprint","IMPRINT",FACE,{"disambiguationData":[TD([[makeQuery(id+"F5.imprint","IMPRINT",EDGE,{"disambiguationData":[TD([[subQ1,-1.0]])],"derivedFrom":subQ0}),1.0]])]});}
            var Q3;
            {var subQ0=sQuery(id+"F5.wireOp",EDGE,"E47");var subQ1=makeQuery(id+"F5.imprint","INTERSECT",VERTEX,{"derivedFrom":[subQ0,sQuery(id+"F5.wireOp",EDGE,"E63.trimOffspring")]});Q3=makeQuery(id+"F5.imprint","IMPRINT",FACE,{"disambiguationData":[TD([[makeQuery(id+"F5.imprint","IMPRINT",EDGE,{"disambiguationData":[TD([[subQ1,-1.0]])],"derivedFrom":subQ0}),1.0]])]});}
            var Q4;
            {var subQ0=sQuery(id+"F5.wireOp",EDGE,"E52");var subQ1=makeQuery(id+"F5.imprint","INTERSECT",VERTEX,{"derivedFrom":[subQ0,sQuery(id+"F5.wireOp",EDGE,"E69.trimOffspring")]});Q4=makeQuery(id+"F5.imprint","IMPRINT",FACE,{"disambiguationData":[TD([[makeQuery(id+"F5.imprint","IMPRINT",EDGE,{"disambiguationData":[TD([[subQ1,-1.0]])],"derivedFrom":subQ0}),1.0]])]});}
            var Q5;
            {var subQ0=sQuery(id+"F5.wireOp",EDGE,"E51");var subQ1=makeQuery(id+"F5.imprint","INTERSECT",VERTEX,{"derivedFrom":[subQ0,sQuery(id+"F5.wireOp",EDGE,"E67.trimOffspring")]});Q5=makeQuery(id+"F5.imprint","IMPRINT",FACE,{"disambiguationData":[TD([[makeQuery(id+"F5.imprint","IMPRINT",EDGE,{"disambiguationData":[TD([[subQ1,-1.0]])],"derivedFrom":subQ0}),1.0]])]});}
            var Q6;
            {var subQ0=sQuery(id+"F5.wireOp",EDGE,"E50");var subQ1=makeQuery(id+"F5.imprint","INTERSECT",VERTEX,{"derivedFrom":[subQ0,sQuery(id+"F5.wireOp",EDGE,"E65.trimOffspring")]});Q6=makeQuery(id+"F5.imprint","IMPRINT",FACE,{"disambiguationData":[TD([[makeQuery(id+"F5.imprint","IMPRINT",EDGE,{"disambiguationData":[TD([[subQ1,1.0]])],"derivedFrom":subQ0}),1.0]])]});}
            var Q7;
            {var subQ0=sQuery(id+"F5.wireOp",EDGE,"E49");var subQ1=makeQuery(id+"F5.imprint","INTERSECT",VERTEX,{"derivedFrom":[subQ0,sQuery(id+"F5.wireOp",EDGE,"E59.trimOffspring")]});Q7=makeQuery(id+"F5.imprint","IMPRINT",FACE,{"disambiguationData":[TD([[makeQuery(id+"F5.imprint","IMPRINT",EDGE,{"disambiguationData":[TD([[subQ1,1.0]])],"derivedFrom":subQ0}),1.0]])]});}
            var Q8;
            {var subQ0=sQuery(id+"F5.wireOp",EDGE,"E48");var subQ1=makeQuery(id+"F5.imprint","INTERSECT",VERTEX,{"derivedFrom":[subQ0,sQuery(id+"F5.wireOp",EDGE,"E61.trimOffspring")]});Q8=makeQuery(id+"F5.imprint","IMPRINT",FACE,{"disambiguationData":[TD([[makeQuery(id+"F5.imprint","IMPRINT",EDGE,{"disambiguationData":[TD([[subQ1,-1.0]])],"derivedFrom":subQ0}),1.0]])]});}
            extrude(context, id + "F11", {"entities" : qUnion([Q0, Q1, Q2, Q3, Q4, Q5, Q6, Q7, Q8]), "operationType" : NewBodyOperationType.ADD, "depth" : 5 * mm});
        }
    });
